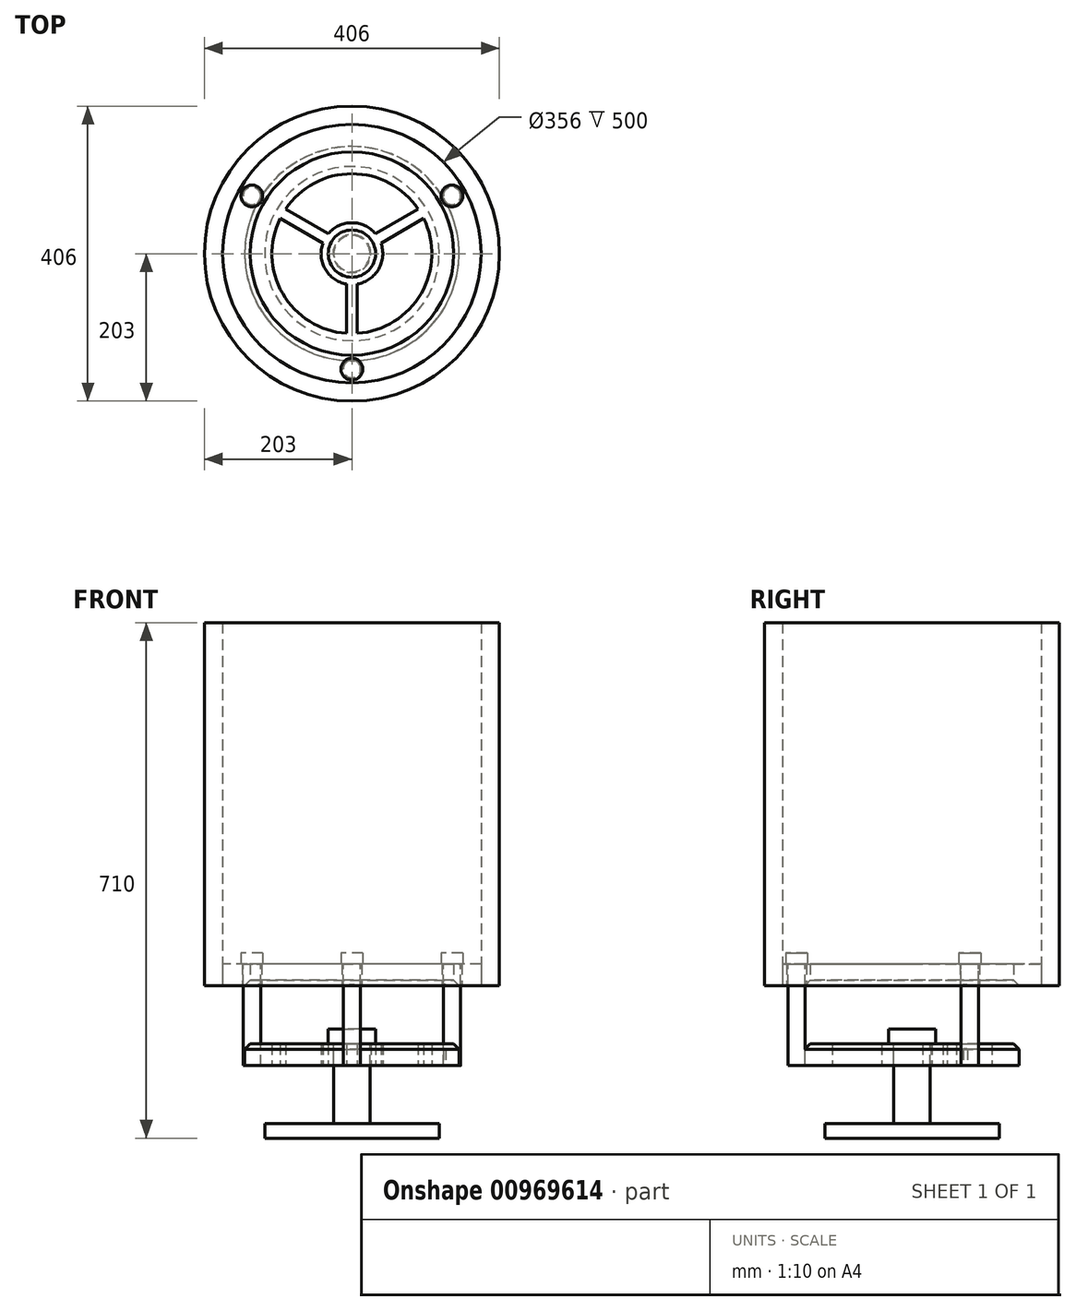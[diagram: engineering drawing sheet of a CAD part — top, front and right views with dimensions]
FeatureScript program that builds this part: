
annotation { "Feature Type Name" : "Feature", "Feature Type Description" : "" }
export const myFeature = defineFeature(function(context is Context, id is Id, definition is map)
    precondition{}
    {
        {
            var Q0;
            Q0=qCreatedBy(makeId("Top.planeOp"),FACE);
            var sketch = newSketch(context, id + "F0", { "sketchPlane" : qUnion([Q0])});
            skCircle(sketch, "E0", {"center": v(0, 0) * mm, "radius": 178 * mm});
            skCircle(sketch, "E1", {"center": v(0, 0) * mm, "radius": 140 * mm});
            skCircle(sketch, "E2", {"center": v(0, 0) * mm, "radius": 159 * mm, "construction": true});
            skCircle(sketch, "E3", {"center": v(0, -159) * mm, "radius": 13.5 * mm});
            skCircle(sketch, "E4.1.0", {"center": v(137.7, 79.5) * mm, "radius": 13.5 * mm});
            skCircle(sketch, "E4.2.0", {"center": v(-137.7, 79.5) * mm, "radius": 13.5 * mm});
            skSolve(sketch);
        }
        {
            var Q0;
            Q0=makeQuery(id+"F0.imprint","IMPRINT",FACE,{"disambiguationData":[TD([[makeQuery(id+"F0.imprint","IMPRINT",EDGE,{"derivedFrom":sQuery(id+"F0.wireOp",EDGE,"E1")}),-1.0]])]});
            extrude(context, id + "F1", {"entities" : qUnion([Q0]), "depth" : 30 * mm, "offsetDistance" : 25 * mm});
        }
        {
            var Q0;
            Q0=makeQuery(id+"F1.opExtrude","CAP_EDGE",EDGE,{"disambiguationData":[OSD([sQuery(id+"F0.wireOp",EDGE,"E1")])],"isStart":true});
            chamfer(context, id + "F2", {"entities" : qUnion([Q0]), "width" : 7.5 * mm, "tangentPropagation" : true});
        }
        {
            var Q0;
            Q0=makeQuery(id+"F0.imprint","IMPRINT",FACE,{"disambiguationData":[TD([[makeQuery(id+"F0.imprint","IMPRINT",EDGE,{"derivedFrom":sQuery(id+"F0.wireOp",EDGE,"E1")}),1.0]])]});
            var sketch = newSketch(context, id + "F3", { "sketchPlane" : qUnion([Q0])});
            skCircle(sketch, "E5", {"center": v(0, 0) * mm, "radius": 203 * mm});
            skCircle(sketch, "E6", {"center": v(0, 0) * mm, "radius": 178 * mm});
            skSolve(sketch);
        }
        {
            var Q0;
            Q0 = qSketchRegion(id + "F3", true);
            extrude(context, id + "F4", {"entities" : qUnion([Q0]), "depth" : 500 * mm, "offsetDistance" : 25 * mm});
        }
        {
            var Q0;
            Q0=makeQuery(id+"F1.opExtrude","CAP_FACE",FACE,{"disambiguationData":[OSD([sQuery(id+"F0.wireOp",EDGE,"E1"),sQuery(id+"F0.wireOp",EDGE,"E0"),sQuery(id+"F0.wireOp",EDGE,"E3"),sQuery(id+"F0.wireOp",EDGE,"E4.1.0"),sQuery(id+"F0.wireOp",EDGE,"E4.2.0")])],"isStart":false});
            var sketch = newSketch(context, id + "F5", { "sketchPlane" : qUnion([Q0])});
            skCircle(sketch, "E7", {"center": v(137.7, 79.5) * mm, "radius": 15 * mm});
            skCircle(sketch, "E8", {"center": v(0, 0) * mm, "radius": 159 * mm, "construction": true});
            skCircle(sketch, "E9.1.0", {"center": v(0, -159) * mm, "radius": 15 * mm});
            skCircle(sketch, "E9.2.0", {"center": v(-137.7, 79.5) * mm, "radius": 15 * mm});
            skLineSegment(sketch, "E9.anchor1", {"start": v(0, 0) * mm, "end": v(137.7, 79.5) * mm, "construction": true});
            skLineSegment(sketch, "E9.anchor2", {"start": v(0, 0) * mm, "end": v(-137.7, 79.5) * mm, "construction": true});
            skCircle(sketch, "E10", {"center": v(137.7, 79.5) * mm, "radius": 12 * mm});
            skCircle(sketch, "E11.1.0", {"center": v(-137.7, 79.5) * mm, "radius": 12 * mm});
            skCircle(sketch, "E11.2.0", {"center": v(0, -159) * mm, "radius": 12 * mm});
            skSolve(sketch);
        }
        {
            var Q0;
            Q0=makeQuery(id+"F5.imprint","IMPRINT",FACE,{"disambiguationData":[TD([[makeQuery(id+"F5.imprint","IMPRINT",EDGE,{"derivedFrom":sQuery(id+"F5.wireOp",EDGE,"E10")}),1.0]])]});
            var Q1;
            Q1=makeQuery(id+"F5.imprint","IMPRINT",FACE,{"disambiguationData":[TD([[makeQuery(id+"F5.imprint","IMPRINT",EDGE,{"derivedFrom":sQuery(id+"F5.wireOp",EDGE,"E10")}),-1.0]])]});
            var Q2;
            Q2=makeQuery(id+"F5.imprint","IMPRINT",FACE,{"disambiguationData":[TD([[makeQuery(id+"F5.imprint","IMPRINT",EDGE,{"derivedFrom":sQuery(id+"F5.wireOp",EDGE,"E7")}),1.0]])]});
            var Q3;
            Q3=makeQuery(id+"F5.imprint","IMPRINT",FACE,{"disambiguationData":[TD([[makeQuery(id+"F5.imprint","IMPRINT",EDGE,{"derivedFrom":sQuery(id+"F5.wireOp",EDGE,"E11.1.0")}),1.0]])]});
            var Q4;
            Q4=makeQuery(id+"F5.imprint","IMPRINT",FACE,{"disambiguationData":[TD([[makeQuery(id+"F5.imprint","IMPRINT",EDGE,{"derivedFrom":sQuery(id+"F5.wireOp",EDGE,"E11.1.0")}),-1.0]])]});
            var Q5;
            Q5=makeQuery(id+"F5.imprint","IMPRINT",FACE,{"disambiguationData":[TD([[makeQuery(id+"F5.imprint","IMPRINT",EDGE,{"derivedFrom":sQuery(id+"F5.wireOp",EDGE,"E9.2.0")}),1.0]])]});
            var Q6;
            Q6=makeQuery(id+"F5.imprint","IMPRINT",FACE,{"disambiguationData":[TD([[makeQuery(id+"F5.imprint","IMPRINT",EDGE,{"derivedFrom":sQuery(id+"F5.wireOp",EDGE,"E11.2.0")}),1.0]])]});
            var Q7;
            Q7=makeQuery(id+"F5.imprint","IMPRINT",FACE,{"disambiguationData":[TD([[makeQuery(id+"F5.imprint","IMPRINT",EDGE,{"derivedFrom":sQuery(id+"F5.wireOp",EDGE,"E11.2.0")}),-1.0]])]});
            var Q8;
            Q8=makeQuery(id+"F5.imprint","IMPRINT",FACE,{"disambiguationData":[TD([[makeQuery(id+"F5.imprint","IMPRINT",EDGE,{"derivedFrom":sQuery(id+"F5.wireOp",EDGE,"E9.1.0")}),1.0]])]});
            extrude(context, id + "F6", {"entities" : qUnion([Q0, Q1, Q2, Q3, Q4, Q5, Q6, Q7, Q8]), "depth" : 15 * mm, "offsetDistance" : 25 * mm});
        }
        {
            var Q0;
            Q0=makeQuery(id+"F5.imprint","IMPRINT",FACE,{"disambiguationData":[TD([[makeQuery(id+"F5.imprint","IMPRINT",EDGE,{"derivedFrom":sQuery(id+"F5.wireOp",EDGE,"E11.2.0")}),1.0]])]});
            var Q1;
            Q1=makeQuery(id+"F5.imprint","IMPRINT",FACE,{"disambiguationData":[TD([[makeQuery(id+"F5.imprint","IMPRINT",EDGE,{"derivedFrom":sQuery(id+"F5.wireOp",EDGE,"E11.1.0")}),1.0]])]});
            var Q2;
            Q2=makeQuery(id+"F5.imprint","IMPRINT",FACE,{"disambiguationData":[TD([[makeQuery(id+"F5.imprint","IMPRINT",EDGE,{"derivedFrom":sQuery(id+"F5.wireOp",EDGE,"E10")}),1.0]])]});
            extrude(context, id + "F7", {"entities" : qUnion([Q0, Q1, Q2]), "operationType" : NewBodyOperationType.ADD, "oppositeDirection" : true, "depth" : 140 * mm, "offsetDistance" : 25 * mm});
        }
        {
            var Q0;
            Q0=makeQuery(id+"F7.opExtrude","CAP_FACE",FACE,{"disambiguationData":[OSD([sQuery(id+"F5.wireOp",EDGE,"E10")])],"isStart":false});
            var sketch = newSketch(context, id + "F8", { "sketchPlane" : qUnion([Q0])});
            skCircle(sketch, "E12", {"center": v(0, 0) * mm, "radius": 147.5 * mm});
            skCircle(sketch, "E13", {"center": v(0, 0) * mm, "radius": 110 * mm});
            skCircle(sketch, "E14", {"center": v(0, 0) * mm, "radius": 42.5 * mm});
            skLineSegment(sketch, "E15.0", {"start": v(7.5, 41.83) * mm, "end": v(7.5, 109.74) * mm});
            skLineSegment(sketch, "E16.0", {"start": v(-7.5, 41.83) * mm, "end": v(-7.5, 109.74) * mm});
            skLineSegment(sketch, "E17.1.0", {"start": v(-32.48, -27.41) * mm, "end": v(-91.3, -61.37) * mm});
            skLineSegment(sketch, "E17.1.1", {"start": v(-39.98, -14.42) * mm, "end": v(-98.8, -48.38) * mm});
            skLineSegment(sketch, "E17.2.0", {"start": v(39.98, -14.42) * mm, "end": v(98.8, -48.38) * mm});
            skLineSegment(sketch, "E17.2.1", {"start": v(32.48, -27.41) * mm, "end": v(91.3, -61.37) * mm});
            skSolve(sketch);
        }
        {
            var Q0;
            {var subQ0=sQuery(id+"F8.wireOp",EDGE,"E12");var subQ1=makeQuery(id+"F7.opExtrude","CAP_EDGE",EDGE,{"disambiguationData":[OSD([sQuery(id+"F5.wireOp",EDGE,"E10")])],"isStart":false});var subQ2=makeQuery(id+"F8.imprint","INTERSECT",VERTEX,{"disambiguationData":[OD(0.0)],"derivedFrom":[subQ1,subQ0]});Q0=makeQuery(id+"F8.imprint","IMPRINT",FACE,{"disambiguationData":[TD([[makeQuery(id+"F8.imprint","IMPRINT",EDGE,{"disambiguationData":[TD([[subQ2,1.0]])],"derivedFrom":subQ0}),1.0]])]});}
            extrude(context, id + "F9", {"entities" : qUnion([Q0]), "oppositeDirection" : true, "depth" : 30 * mm, "offsetDistance" : 25 * mm});
        }
        {
            var Q0;
            Q0=makeQuery(id+"F9.opExtrude","CAP_EDGE",EDGE,{"disambiguationData":[OSD([sQuery(id+"F8.wireOp",EDGE,"E12")])],"isStart":false});
            chamfer(context, id + "F10", {"entities" : qUnion([Q0]), "width" : 7.5 * mm, "tangentPropagation" : true});
        }
        {
            var Q0;
            {var subQ0=sQuery(id+"F8.wireOp",EDGE,"E17.2.0");Q0=makeQuery(id+"F8.imprint","IMPRINT",FACE,{"disambiguationData":[TD([[makeQuery(id+"F8.imprint","IMPRINT",EDGE,{"derivedFrom":subQ0}),-1.0]])]});}
            var Q1;
            {var subQ0=sQuery(id+"F8.wireOp",EDGE,"E17.1.0");Q1=makeQuery(id+"F8.imprint","IMPRINT",FACE,{"disambiguationData":[TD([[makeQuery(id+"F8.imprint","IMPRINT",EDGE,{"derivedFrom":subQ0}),-1.0]])]});}
            var Q2;
            {var subQ0=sQuery(id+"F8.wireOp",EDGE,"E14");var subQ5=makeQuery(id+"F8.imprint","INTERSECT",VERTEX,{"derivedFrom":[subQ0,sQuery(id+"F8.wireOp",EDGE,"E15.0")]});Q2=makeQuery(id+"F8.imprint","IMPRINT",FACE,{"disambiguationData":[TD([[makeQuery(id+"F8.imprint","IMPRINT",EDGE,{"disambiguationData":[TD([[subQ5,-1.0]])],"derivedFrom":subQ0}),1.0]])]});}
            var Q3;
            {var subQ0=sQuery(id+"F8.wireOp",EDGE,"E15.0");Q3=makeQuery(id+"F8.imprint","IMPRINT",FACE,{"disambiguationData":[TD([[makeQuery(id+"F8.imprint","IMPRINT",EDGE,{"derivedFrom":subQ0}),1.0]])]});}
            extrude(context, id + "F11", {"entities" : qUnion([Q0, Q1, Q2, Q3]), "operationType" : NewBodyOperationType.ADD, "oppositeDirection" : true, "depth" : 30 * mm, "offsetDistance" : 25 * mm});
        }
        {
            var Q0;
            Q0=sQuery(id+"F8.wireOp",VERTEX,"E12.center");
            var Q1;
            Q1=makeQuery(id+"F9.opExtrude","SWEPT_BODY",BODY,{"disambiguationData":[OSD([sQuery(id+"F5.wireOp",EDGE,"E10"),sQuery(id+"F8.wireOp",EDGE,"E12"),sQuery(id+"F8.wireOp",EDGE,"E13")])]});
            hole(context, id + "F12", {"style" : HoleStyle.SIMPLE, "endStyle" : HoleEndStyle.THROUGH, "holeDiameter" : 52 * mm, "majorDiameter" : 5 * mm, "isTappedThrough" : true, "tappedDepth" : 12 * mm, "tapClearance" : 3, "locations" : qUnion([Q0]), "scope" : qUnion([Q1])});
        }
        {
            var Q0;
            {var subQ0=sQuery(id+"F8.wireOp",EDGE,"E13");Q0=makeQuery(id+"F11.boolean.opBoolean","MERGE",FACE,{"derivedFrom":[makeQuery(id+"F9.opExtrude","CAP_FACE",FACE,{"disambiguationData":[OSD([sQuery(id+"F5.wireOp",EDGE,"E10"),sQuery(id+"F8.wireOp",EDGE,"E12"),subQ0])],"isStart":false}),makeQuery(id+"F11.opExtrude","CAP_FACE",FACE,{"disambiguationData":[OSD([subQ0,sQuery(id+"F8.wireOp",EDGE,"E14"),sQuery(id+"F8.wireOp",EDGE,"E15.0"),sQuery(id+"F8.wireOp",EDGE,"E16.0"),sQuery(id+"F8.wireOp",EDGE,"E17.1.0"),sQuery(id+"F8.wireOp",EDGE,"E17.1.1"),sQuery(id+"F8.wireOp",EDGE,"E17.2.0"),sQuery(id+"F8.wireOp",EDGE,"E17.2.1")])],"isStart":false})]});}
            var sketch = newSketch(context, id + "F13", { "sketchPlane" : qUnion([Q0])});
            skCircle(sketch, "E18", {"center": v(0, 0) * mm, "radius": 32.5 * mm});
            skCircle(sketch, "E19", {"center": v(0, 0) * mm, "radius": 25 * mm});
            skSolve(sketch);
        }
        {
            var Q0;
            Q0=makeQuery(id+"F13.imprint","IMPRINT",FACE,{"disambiguationData":[TD([[makeQuery(id+"F13.imprint","IMPRINT",EDGE,{"derivedFrom":sQuery(id+"F13.wireOp",EDGE,"E18")}),1.0]])]});
            var Q1;
            Q1=makeQuery(id+"F13.imprint","IMPRINT",FACE,{"disambiguationData":[TD([[makeQuery(id+"F13.imprint","IMPRINT",EDGE,{"derivedFrom":sQuery(id+"F13.wireOp",EDGE,"E19")}),-1.0]])]});
            var Q2;
            Q2=makeQuery(id+"F13.imprint","IMPRINT",FACE,{"disambiguationData":[TD([[makeQuery(id+"F13.imprint","IMPRINT",EDGE,{"derivedFrom":sQuery(id+"F13.wireOp",EDGE,"E19")}),1.0]])]});
            extrude(context, id + "F14", {"entities" : qUnion([Q0, Q1, Q2]), "depth" : 20 * mm, "offsetDistance" : 25 * mm});
        }
        {
            var Q0;
            Q0=makeQuery(id+"F13.imprint","IMPRINT",FACE,{"disambiguationData":[TD([[makeQuery(id+"F13.imprint","IMPRINT",EDGE,{"derivedFrom":sQuery(id+"F13.wireOp",EDGE,"E19")}),1.0]])]});
            extrude(context, id + "F15", {"entities" : qUnion([Q0]), "operationType" : NewBodyOperationType.ADD, "oppositeDirection" : true, "depth" : 110 * mm, "offsetDistance" : 25 * mm});
        }
        {
            var Q0;
            Q0=makeQuery(id+"F15.opExtrude","CAP_FACE",FACE,{"disambiguationData":[OSD([sQuery(id+"F13.wireOp",EDGE,"E19")])],"isStart":false});
            var sketch = newSketch(context, id + "F16", { "sketchPlane" : qUnion([Q0])});
            skCircle(sketch, "E20", {"center": v(0, 0) * mm, "radius": 120 * mm});
            skSolve(sketch);
        }
        {
            var Q0;
            Q0 = qSketchRegion(id + "F16", true);
            extrude(context, id + "F17", {"entities" : qUnion([Q0]), "depth" : 20 * mm, "offsetDistance" : 25 * mm});
        }
    });
